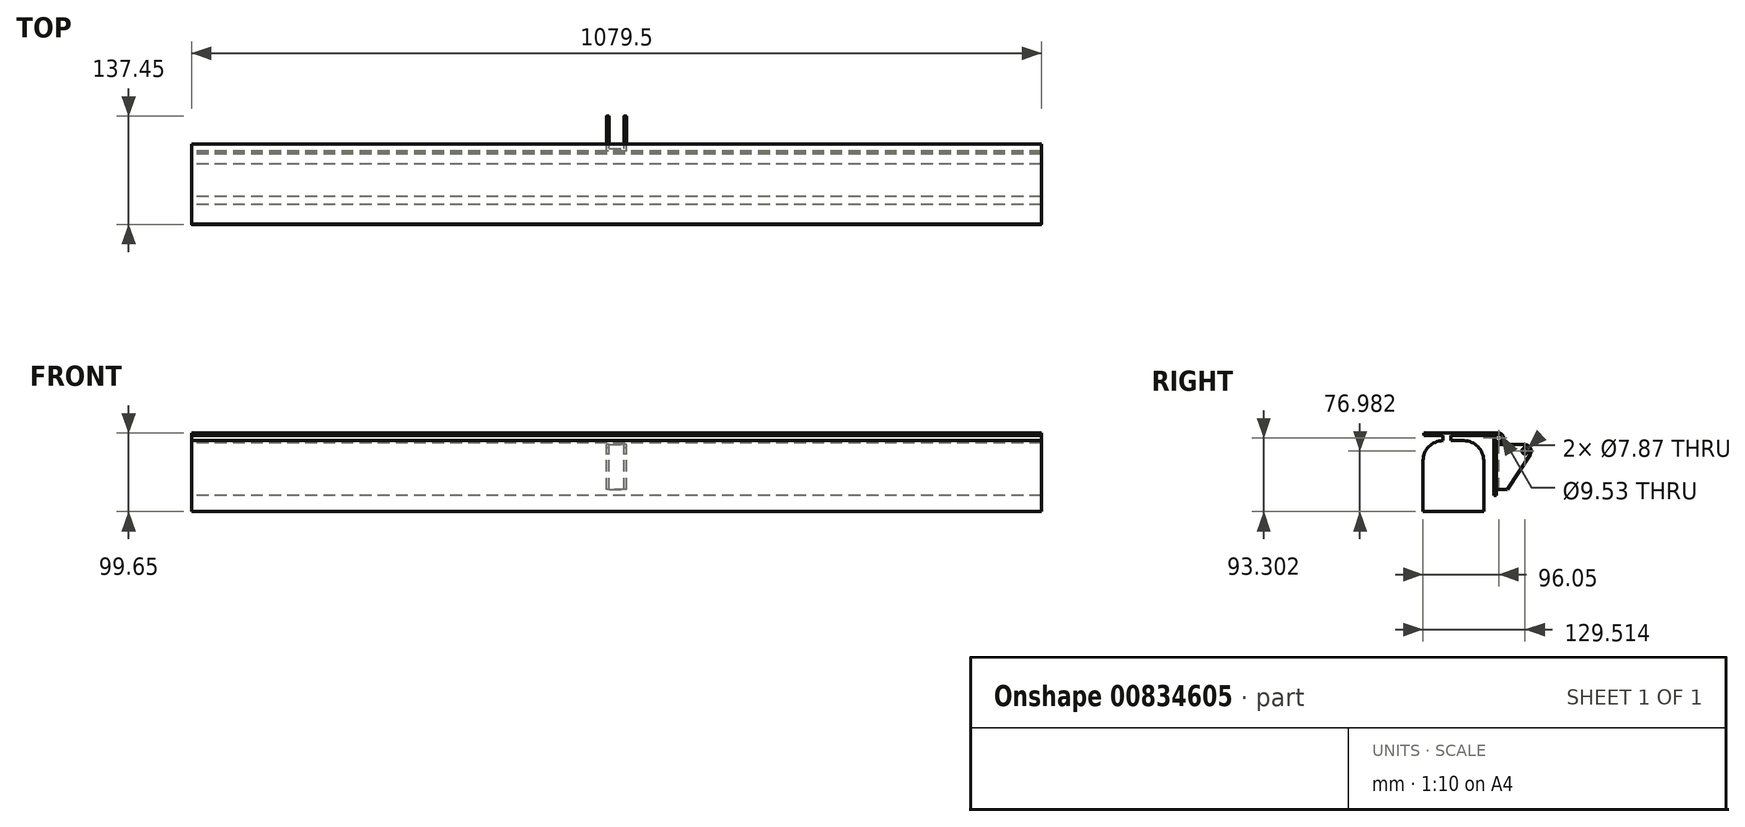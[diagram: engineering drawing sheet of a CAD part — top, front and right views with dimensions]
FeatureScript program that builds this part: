
annotation { "Feature Type Name" : "Feature", "Feature Type Description" : "" }
export const myFeature = defineFeature(function(context is Context, id is Id, definition is map)
    precondition{}
    {
        {
            var Q0;
            Q0=qCreatedBy(makeId("Right.planeOp"),FACE);
            var sketch = newSketch(context, id + "F0", { "sketchPlane" : qUnion([Q0])});
            skLineSegment(sketch, "E0.bottom", {"start": v(0, 0) * mm, "end": v(-54.34, 0) * mm});
            skLineSegment(sketch, "E0.top", {"start": v(12.7, 3.3) * mm, "end": v(-88.9, 3.3) * mm});
            skLineSegment(sketch, "E0.right", {"start": v(-88.9, 0) * mm, "end": v(-88.9, 3.3) * mm});
            skLineSegment(sketch, "E1.bottom", {"start": v(-76.96, 0) * mm, "end": v(-64.3, 0) * mm});
            skLineSegment(sketch, "E2", {"start": v(-38.1, 3.3) * mm, "end": v(-38.1, -86.53) * mm, "construction": true});
            skPoint(sketch, "E3.snap10", {"position": v(-44.45, 0) * mm});
            skLineSegment(sketch, "E4", {"start": v(0, -50.8) * mm, "end": v(0, -75.98) * mm, "construction": true});
            skLineSegment(sketch, "E5.bottom", {"start": v(-54.34, -6.35) * mm, "end": v(-38.1, -6.35) * mm});
            skLineSegment(sketch, "E5.top", {"start": v(-89.7, -96.35) * mm, "end": v(-12.7, -96.35) * mm});
            skLineSegment(sketch, "E5.left", {"start": v(-89.7, -31.75) * mm, "end": v(-89.7, -96.35) * mm});
            skLineSegment(sketch, "E5.right", {"start": v(-12.7, -31.75) * mm, "end": v(-12.7, -96.35) * mm});
            skPoint(sketch, "E6.visualSharp", {"position": v(-89.7, -6.35) * mm});
            skArc(sketch, "E6.filletArc", {"start": v(-64.3, -6.35) * mm, "mid": v(-82.26, -13.79) * mm, "end": v(-89.7, -31.75) * mm});
            skPoint(sketch, "E7.visualSharp", {"position": v(-12.7, -6.35) * mm});
            skArc(sketch, "E7.filletArc", {"start": v(-12.7, -31.75) * mm, "mid": v(-20.14, -13.79) * mm, "end": v(-38.1, -6.35) * mm});
            skArc(sketch, "E8", {"start": v(3.3, -8.62) * mm, "mid": v(12.5, -4.62) * mm, "end": v(6.35, 3.3) * mm});
            skCircle(sketch, "E9", {"center": v(6.35, -3.05) * mm, "radius": 4.76 * mm});
            skLineSegment(sketch, "E10", {"start": v(6.35, 3.3) * mm, "end": v(12.7, 3.3) * mm});
            skLineSegment(sketch, "E11", {"start": v(0, 0) * mm, "end": v(0, -3.05) * mm});
            skLineSegment(sketch, "E12.bottom", {"start": v(0, -75.98) * mm, "end": v(3.3, -75.98) * mm});
            skLineSegment(sketch, "E12.left", {"start": v(0, -75.98) * mm, "end": v(0, -8.62) * mm});
            skLineSegment(sketch, "E12.right", {"start": v(3.3, -75.98) * mm, "end": v(3.3, -8.62) * mm});
            skLineSegment(sketch, "E13", {"start": v(0, -3.05) * mm, "end": v(0, -8.62) * mm});
            skLineSegment(sketch, "E14", {"start": v(6.35, -3.05) * mm, "end": v(6.35, 12.8) * mm, "construction": true});
            skLineSegment(sketch, "E15", {"start": v(6.35, 12.8) * mm, "end": v(6.35, -3.05) * mm, "construction": true});
            skLineSegment(sketch, "E16", {"start": v(20.47, -3.05) * mm, "end": v(6.35, -3.05) * mm, "construction": true});
            skLineSegment(sketch, "E17.left", {"start": v(-64.3, -6.35) * mm, "end": v(-64.3, 0) * mm});
            skLineSegment(sketch, "E17.right", {"start": v(-54.34, -6.35) * mm, "end": v(-54.34, 0) * mm});
            skLineSegment(sketch, "E18.trimOffspring", {"start": v(-54.34, 0) * mm, "end": v(-11.94, 0) * mm});
            skLineSegment(sketch, "E19.trimOffspring", {"start": v(-64.3, 0) * mm, "end": v(-88.9, 0) * mm});
            skCircle(sketch, "E20", {"center": v(6.35, -3.05) * mm, "radius": 6.35 * mm, "construction": true});
            skSolve(sketch);
        }
        {
            var Q0;
            Q0=makeQuery(id+"F0.imprint","IMPRINT",FACE,{"disambiguationData":[TD([[makeQuery(id+"F0.imprint","IMPRINT",EDGE,{"derivedFrom":sQuery(id+"F0.wireOp",EDGE,"E1.top")}),1.0]])]});
            var Q1;
            Q1=makeQuery(id+"F0.imprint","IMPRINT",FACE,{"disambiguationData":[TD([[makeQuery(id+"F0.imprint","IMPRINT",EDGE,{"derivedFrom":sQuery(id+"F0.wireOp",EDGE,"E0.top")}),1.0]])]});
            var Q2;
            {var subQ0=sQuery(id+"F0.wireOp",EDGE,"4fJF9v0Z-RCyY-sMw6-P9Y5-TZvlafu2ZhkZ");Q2=makeQuery(id+"F0.imprint","IMPRINT",FACE,{"disambiguationData":[TD([[makeQuery(id+"F0.imprint","IMPRINT",EDGE,{"derivedFrom":subQ0}),1.0]])]});}
            var Q3;
            Q3=makeQuery(id+"F0.imprint","IMPRINT",FACE,{"disambiguationData":[TD([[makeQuery(id+"F0.imprint","IMPRINT",EDGE,{"derivedFrom":sQuery(id+"F0.wireOp",EDGE,"p42B6GDp-Gyb2-AZrX-nPjD-DgscU1KKJdLw")}),-1.0]])]});
            var Q4;
            Q4=makeQuery(id+"F0.imprint","IMPRINT",FACE,{"disambiguationData":[TD([[makeQuery(id+"F0.imprint","IMPRINT",EDGE,{"derivedFrom":sQuery(id+"F0.wireOp",EDGE,"5w4a5uff-Vtlf-AeRg-57yw-sYJzRJ06lHgg")}),-1.0]])]});
            var Q5;
            {var subQ0=sQuery(id+"F0.wireOp",EDGE,"E0.left");Q5=makeQuery(id+"F0.imprint","IMPRINT",FACE,{"disambiguationData":[TD([[makeQuery(id+"F0.imprint","IMPRINT",EDGE,{"derivedFrom":subQ0}),-1.0]])]});}
            var Q6;
            Q6=makeQuery(id+"F0.imprint","IMPRINT",FACE,{"disambiguationData":[TD([[makeQuery(id+"F0.imprint","IMPRINT",EDGE,{"derivedFrom":sQuery(id+"F0.wireOp",EDGE,"E5.bottom")}),-1.0]])]});
            extrude(context, id + "F1", {"entities" : qUnion([Q0, Q1, Q2, Q3, Q4, Q5, Q6]), "depth" : 1079.5 * mm, "offsetDistance" : 25.4 * mm});
        }
        {
            var Q0;
            Q0=qCreatedBy(makeId("Right.planeOp"),FACE);
            cPlane(context, id + "F2", {"entities" : qUnion([Q0]), "cplaneType" : CPlaneType.OFFSET, "offset" : 539.75 * mm, "width" : 152.4 * mm, "height" : 152.4 * mm});
        }
        {
            var Q0;
            Q0=qCreatedBy(id+"F2.planeOp",FACE);
            var sketch = newSketch(context, id + "F3", { "sketchPlane" : qUnion([Q0])});
            skLineSegment(sketch, "E21.bottom", {"start": v(3.3, -68.58) * mm, "end": v(17.59, -68.58) * mm});
            skLineSegment(sketch, "E21.top", {"start": v(3.3, -11.43) * mm, "end": v(39.81, -11.43) * mm});
            skLineSegment(sketch, "E21.left", {"start": v(3.3, -68.58) * mm, "end": v(3.3, -11.43) * mm});
            skCircle(sketch, "E22", {"center": v(39.81, -19.37) * mm, "radius": 3.94 * mm});
            skLineSegment(sketch, "E23", {"start": v(17.59, -68.58) * mm, "end": v(46.49, -23.66) * mm});
            skArc(sketch, "E24", {"start": v(46.49, -23.66) * mm, "mid": v(46.78, -15.57) * mm, "end": v(39.81, -11.43) * mm});
            skSolve(sketch);
        }
        {
            var Q0;
            Q0=makeQuery(id+"F3.imprint","IMPRINT",FACE,{"disambiguationData":[TD([[makeQuery(id+"F3.imprint","IMPRINT",EDGE,{"derivedFrom":sQuery(id+"F3.wireOp",EDGE,"E21.bottom")}),1.0]])]});
            extrude(context, id + "F4", {"entities" : qUnion([Q0]), "operationType" : NewBodyOperationType.ADD, "depth" : 12.7 * mm, "offsetDistance" : 25.4 * mm, "hasSecondDirection" : true, "secondDirectionOppositeDirection" : true, "secondDirectionDepth" : 12.7 * mm});
        }
        {
            var Q0;
            Q0=makeQuery(id+"F4.opExtrude","SWEPT_FACE",FACE,{"disambiguationData":[OSD([sQuery(id+"F3.wireOp",EDGE,"E21.top")])]});
            var sketch = newSketch(context, id + "F5", { "sketchPlane" : qUnion([Q0])});
            skLineSegment(sketch, "E25.bottom", {"start": v(530.23, 6.48) * mm, "end": v(549.27, 6.48) * mm});
            skLineSegment(sketch, "E25.top", {"start": v(530.23, 66.92) * mm, "end": v(549.27, 66.92) * mm});
            skLineSegment(sketch, "E25.left", {"start": v(530.23, 6.48) * mm, "end": v(530.23, 66.92) * mm});
            skLineSegment(sketch, "E25.right", {"start": v(549.27, 6.48) * mm, "end": v(549.27, 66.92) * mm});
            skSolve(sketch);
        }
        {
            var Q0;
            Q0 = qSketchRegion(id + "F5", true);
            extrude(context, id + "F6", {"entities" : qUnion([Q0]), "operationType" : NewBodyOperationType.REMOVE, "endBound" : BoundingType.THROUGH_ALL, "oppositeDirection" : true, "depth" : 25.4 * mm, "offsetDistance" : 25.4 * mm});
        }
    });
